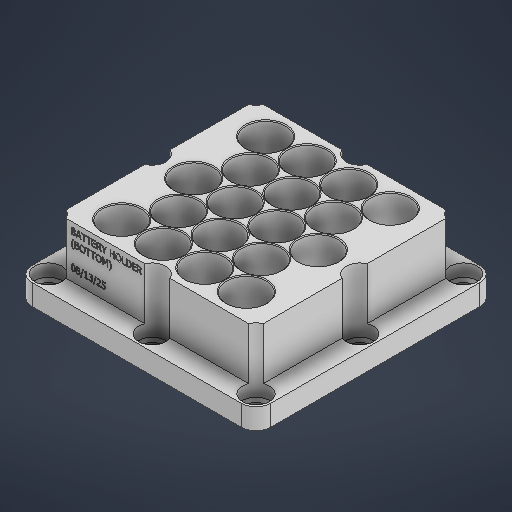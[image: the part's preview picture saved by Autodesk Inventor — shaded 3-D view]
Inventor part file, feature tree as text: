
AUTODESK INVENTOR PART (.ipt)
format: ipt  version: 2025 (Build 290162000, 162)  size: 895,488 bytes
history: native  units: in
note: dims shown in document units (in); Inventor stores cm internally (conversion verified against a paired STEP export)
features: sketch x7, extrude x3, hole x1, fillet x1, chamfer x1
ambient origin geometry x8: Origin, YZ Plane, XZ Plane, XY Plane, X Axis, Y Axis, Z Axis, Center Point
bodies: Solid1 (feature_tree)
feature tree (13):
  extrude  "Extrusion1"  Depth=4.5276in
  extrude  "Extrusion2"  Depth=3.7402in
  hole  "Hole3"  [1 undecoded]
  fillet  "Fillet1"  Radius=1.3638in
  chamfer  "Chamfer1"  Distance=0.748in
  extrude  "Extrusion3"  Depth=0.3937in
  sketch  "Sketch1"  dims[d0=4.5276in d1=4.5276in]
  sketch  "Sketch4"  dims[d2=0.3937in d3=0.0in d48=3.7402in]
  sketch  "Sketch Rectangular Pattern11"  dims[d133=2.7276in]
  sketch  "Sketch Rectangular Pattern12"  dims[d134=0.748in]
  sketch  "Sketch5"  dims[d49=3.7402in d57=0.9843in d58=0.0in d124=1.3638in]
  sketch  "Sketch Rectangular Pattern13"  dims[d135=1.5748in d137=0.7874in d138=1.1811in d140=1.3638in d143=0.748in d146=0.3937in d147=0.6819in d148=1.1811in d150=0.7874in d151=0.7874in d153=1.3638in d156=3.937in d157=3.937in d158=0.2756in d159=1.1811in d161=1.9685in d162=1.1811in d164=1.9685in d167=0.2805in d168=0.2362in d169=0.5118in d170=1.2205in d171=90.0deg d172=0.315in d173=0.8108in d174=0.2805in d175=0.0157in d176=0.0787in d177=45.0deg d178=0.0787in d179=0.0in]
  sketch  "Sketch6"  dims[d132=2.3622in]
note: 1 required parameter value undecoded (feature->parameter linkage not recoverable at this tier; creation-order binding heuristic only, values carry confidence <= 0.55)
